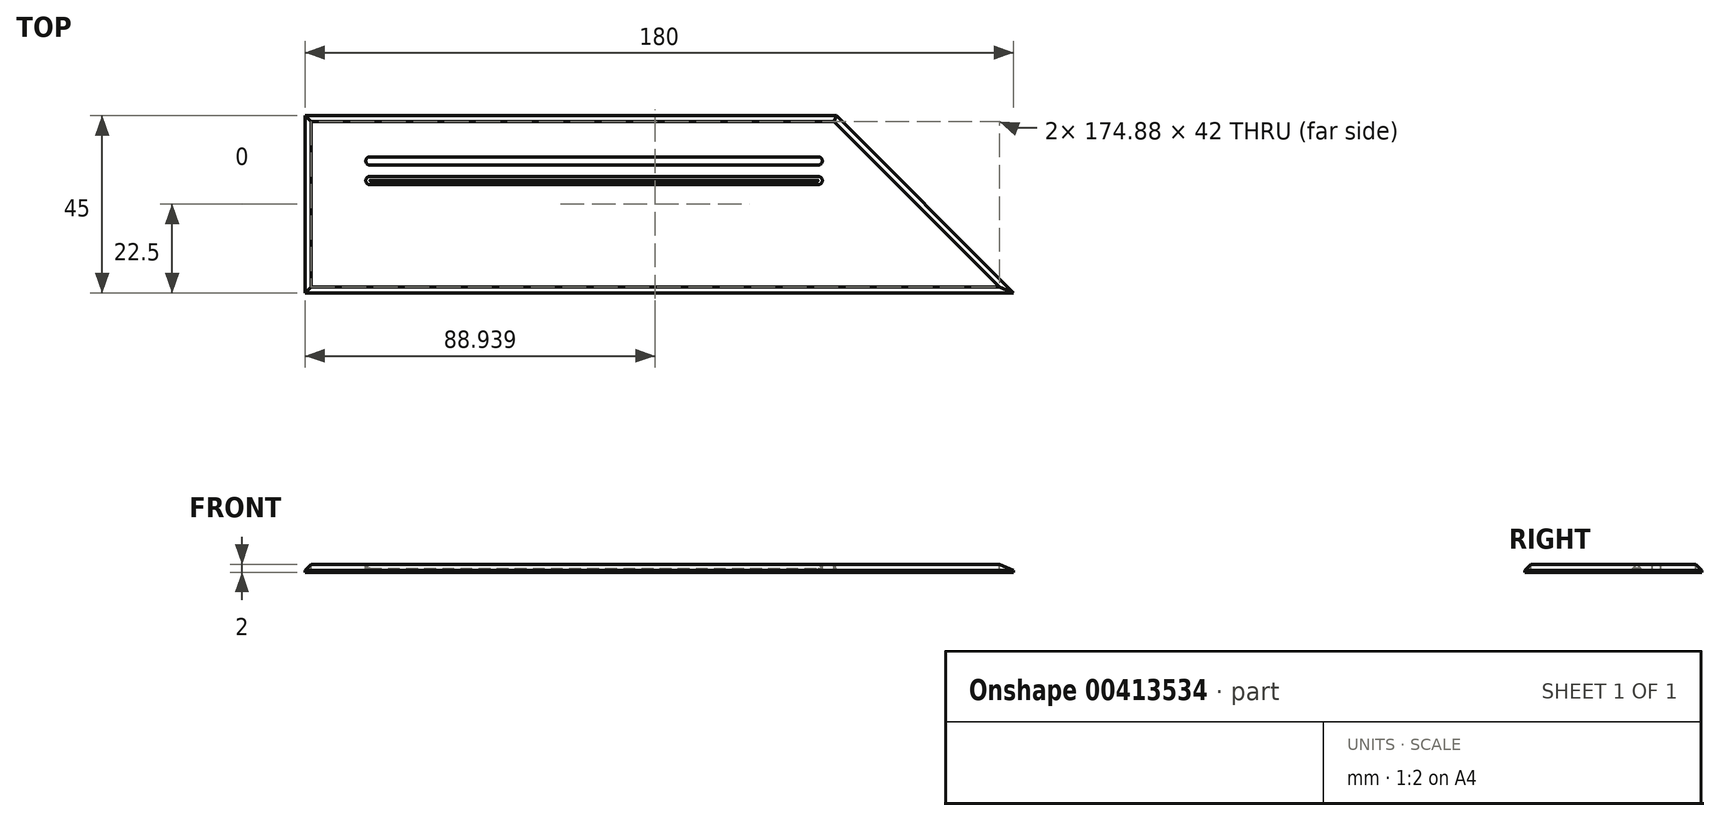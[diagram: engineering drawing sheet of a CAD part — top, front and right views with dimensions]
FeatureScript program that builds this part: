
annotation { "Feature Type Name" : "Feature", "Feature Type Description" : "" }
export const myFeature = defineFeature(function(context is Context, id is Id, definition is map)
    precondition{}
    {
        {
            var Q0;
            Q0=qCreatedBy(makeId("Top.planeOp"),FACE);
            var sketch = newSketch(context, id + "F0", { "sketchPlane" : qUnion([Q0])});
            skLineSegment(sketch, "E0.bottom", {"start": v(67.5, 22.5) * mm, "end": v(-67.5, 22.5) * mm});
            skLineSegment(sketch, "E0.top", {"start": v(112.5, -22.5) * mm, "end": v(-67.5, -22.5) * mm});
            skLineSegment(sketch, "E0.left", {"start": v(67.5, 22.5) * mm, "end": v(112.5, -22.5) * mm});
            skLineSegment(sketch, "E0.right", {"start": v(-67.5, 22.5) * mm, "end": v(-67.5, -22.5) * mm});
            skPoint(sketch, "E0.middle", {"position": v(0, 0) * mm});
            skSolve(sketch);
        }
        {
            var Q0;
            Q0=makeQuery(id+"F0.imprint","IMPRINT",FACE,{"disambiguationData":[TD([[makeQuery(id+"F0.imprint","IMPRINT",EDGE,{"derivedFrom":sQuery(id+"F0.wireOp",EDGE,"E0.bottom")}),1.0]])]});
            extrude(context, id + "F1", {"entities" : qUnion([Q0]), "depth" : 2 * mm});
        }
        {
            var Q0;
            Q0=makeQuery(id+"F1.opExtrude","CAP_EDGE",EDGE,{"disambiguationData":[OSD([sQuery(id+"F0.wireOp",EDGE,"E0.top")])],"isStart":false});
            var Q1;
            Q1=makeQuery(id+"F1.opExtrude","CAP_EDGE",EDGE,{"disambiguationData":[OSD([sQuery(id+"F0.wireOp",EDGE,"E0.right")])],"isStart":false});
            var Q2;
            Q2=makeQuery(id+"F1.opExtrude","CAP_EDGE",EDGE,{"disambiguationData":[OSD([sQuery(id+"F0.wireOp",EDGE,"E0.bottom")])],"isStart":false});
            var Q3;
            Q3=makeQuery(id+"F1.opExtrude","CAP_EDGE",EDGE,{"disambiguationData":[OSD([sQuery(id+"F0.wireOp",EDGE,"E0.left")])],"isStart":false});
            chamfer(context, id + "F2", {"entities" : qUnion([Q0, Q1, Q2, Q3]), "width" : 1.5 * mm, "tangentPropagation" : true});
        }
        {
            var Q0;
            Q0=makeQuery(id+"F1.opExtrude","CAP_FACE",FACE,{"disambiguationData":[OSD([sQuery(id+"F0.wireOp",EDGE,"E0.bottom"),sQuery(id+"F0.wireOp",EDGE,"E0.top"),sQuery(id+"F0.wireOp",EDGE,"E0.left"),sQuery(id+"F0.wireOp",EDGE,"E0.right")])],"isStart":false});
            var sketch = newSketch(context, id + "F3", { "sketchPlane" : qUnion([Q0])});
            skLineSegment(sketch, "E1", {"start": v(-51, 11) * mm, "end": v(62.88, 11) * mm, "construction": true});
            skLineSegment(sketch, "E2", {"start": v(-51, 6) * mm, "end": v(62.88, 6) * mm, "construction": true});
            skArc(sketch, "E3.0.startCap", {"start": v(-51, 9.95) * mm, "mid": v(-52.05, 11) * mm, "end": v(-51, 12.05) * mm});
            skArc(sketch, "E3.0.endCap", {"start": v(62.88, 12.05) * mm, "mid": v(63.93, 11) * mm, "end": v(62.88, 9.95) * mm});
            skLineSegment(sketch, "E3.0.left", {"start": v(-51, 12.05) * mm, "end": v(62.88, 12.05) * mm});
            skLineSegment(sketch, "E3.0.right", {"start": v(-51, 9.95) * mm, "end": v(62.88, 9.95) * mm});
            skArc(sketch, "E3.2.startCap", {"start": v(-51, 4.95) * mm, "mid": v(-52.05, 6) * mm, "end": v(-51, 7.05) * mm});
            skArc(sketch, "E3.2.endCap", {"start": v(62.88, 7.05) * mm, "mid": v(63.93, 6) * mm, "end": v(62.88, 4.95) * mm});
            skLineSegment(sketch, "E3.2.left", {"start": v(-51, 7.05) * mm, "end": v(62.88, 7.05) * mm});
            skLineSegment(sketch, "E3.2.right", {"start": v(-51, 4.95) * mm, "end": v(62.88, 4.95) * mm});
            skLineSegment(sketch, "E4", {"start": v(-51, -9) * mm, "end": v(92.88, -9) * mm, "construction": true});
            skCircle(sketch, "E5", {"center": v(-49, -9) * mm, "radius": 2 * mm});
            skCircle(sketch, "E6", {"center": v(-39, -9) * mm, "radius": 3 * mm});
            skCircle(sketch, "E7", {"center": v(-27, -9) * mm, "radius": 4 * mm});
            skCircle(sketch, "E8", {"center": v(-13, -9) * mm, "radius": 5 * mm});
            skCircle(sketch, "E9", {"center": v(3, -9) * mm, "radius": 6 * mm});
            skEllipse(sketch, "E10", {"center": v(19, -9) * mm, "majorRadius": 2.45 * mm, "minorRadius": 1.41 * mm, "majorAxis": v(-0.7, 0.7)});
            skLineSegment(sketch, "E11", {"start": v(19, -9) * mm, "end": v(17.27, -7.27) * mm, "construction": true});
            skLineSegment(sketch, "E12", {"start": v(21, -7) * mm, "end": v(18, -7) * mm, "construction": true});
            skLineSegment(sketch, "E13", {"start": v(21, -7) * mm, "end": v(21, -10) * mm, "construction": true});
            skEllipse(sketch, "E14", {"center": v(29, -9) * mm, "majorRadius": 3.67 * mm, "minorRadius": 2.12 * mm, "majorAxis": v(-0.7, 0.7)});
            skEllipse(sketch, "E15", {"center": v(42, -9) * mm, "majorRadius": 4.9 * mm, "minorRadius": 2.83 * mm, "majorAxis": v(-0.7, 0.7)});
            skEllipse(sketch, "E16", {"center": v(58, -9) * mm, "majorRadius": 6.12 * mm, "minorRadius": 3.54 * mm, "majorAxis": v(-0.7, 0.7)});
            skEllipse(sketch, "E17", {"center": v(76, -9) * mm, "majorRadius": 7.35 * mm, "minorRadius": 4.24 * mm, "majorAxis": v(-0.7, 0.7)});
            skLineSegment(sketch, "E18", {"start": v(32, -6) * mm, "end": v(27.5, -6) * mm, "construction": true});
            skLineSegment(sketch, "E19", {"start": v(32, -6) * mm, "end": v(32, -10.5) * mm, "construction": true});
            skLineSegment(sketch, "E20", {"start": v(40, -5) * mm, "end": v(46, -5) * mm, "construction": true});
            skLineSegment(sketch, "E21", {"start": v(46, -5) * mm, "end": v(46, -11) * mm, "construction": true});
            skLineSegment(sketch, "E22", {"start": v(55.5, -4) * mm, "end": v(63, -4) * mm, "construction": true});
            skLineSegment(sketch, "E23", {"start": v(63, -4) * mm, "end": v(63, -11.5) * mm, "construction": true});
            skLineSegment(sketch, "E24", {"start": v(73, -3) * mm, "end": v(82, -3) * mm, "construction": true});
            skLineSegment(sketch, "E25", {"start": v(82, -3) * mm, "end": v(82, -12) * mm, "construction": true});
            skLineSegment(sketch, "E26", {"start": v(29, -9) * mm, "end": v(26.4, -6.4) * mm, "construction": true});
            skLineSegment(sketch, "E27", {"start": v(42, -9) * mm, "end": v(38.54, -5.54) * mm, "construction": true});
            skLineSegment(sketch, "E28", {"start": v(58, -9) * mm, "end": v(53.67, -4.67) * mm, "construction": true});
            skLineSegment(sketch, "E29", {"start": v(76, -9) * mm, "end": v(70.8, -3.8) * mm, "construction": true});
            skLineSegment(sketch, "E30.bottom", {"start": v(-56, -6.5) * mm, "end": v(-61, -6.5) * mm});
            skLineSegment(sketch, "E30.top", {"start": v(-56, -11.5) * mm, "end": v(-61, -11.5) * mm});
            skLineSegment(sketch, "E30.left", {"start": v(-56, -6.5) * mm, "end": v(-56, -11.5) * mm});
            skLineSegment(sketch, "E30.right", {"start": v(-61, -6.5) * mm, "end": v(-61, -11.5) * mm});
            skLineSegment(sketch, "E31", {"start": v(-51, 11) * mm, "end": v(-51, -9) * mm, "construction": true});
            skLineSegment(sketch, "E32", {"start": v(62.88, 11) * mm, "end": v(62.88, 6) * mm, "construction": true});
            skLineSegment(sketch, "E33.bottom", {"start": v(-61, 11) * mm, "end": v(-56, 11) * mm});
            skLineSegment(sketch, "E33.top", {"start": v(-61, 6) * mm, "end": v(-56, 6) * mm});
            skLineSegment(sketch, "E33.left", {"start": v(-61, 11) * mm, "end": v(-61, 6) * mm});
            skLineSegment(sketch, "E33.right", {"start": v(-56, 11) * mm, "end": v(-56, 6) * mm});
            skSolve(sketch);
        }
        {
            var Q0;
            Q0=makeQuery(id+"F3.imprint","IMPRINT",FACE,{"disambiguationData":[TD([[makeQuery(id+"F3.imprint","IMPRINT",EDGE,{"derivedFrom":sQuery(id+"F3.wireOp",EDGE,"E33.bottom")}),-1.0]])]});
            var Q1;
            Q1=makeQuery(id+"F3.imprint","IMPRINT",FACE,{"disambiguationData":[TD([[makeQuery(id+"F3.imprint","IMPRINT",EDGE,{"derivedFrom":sQuery(id+"F3.wireOp",EDGE,"E3.0.startCap")}),-1.0]])]});
            var Q2;
            Q2=makeQuery(id+"F3.imprint","IMPRINT",FACE,{"disambiguationData":[TD([[makeQuery(id+"F3.imprint","IMPRINT",EDGE,{"derivedFrom":sQuery(id+"F3.wireOp",EDGE,"E3.2.startCap")}),-1.0]])]});
            var Q3;
            Q3=makeQuery(id+"F3.imprint","IMPRINT",FACE,{"disambiguationData":[TD([[makeQuery(id+"F3.imprint","IMPRINT",EDGE,{"derivedFrom":sQuery(id+"F3.wireOp",EDGE,"E30.bottom")}),1.0]])]});
            var Q4;
            Q4=makeQuery(id+"F3.imprint","IMPRINT",FACE,{"disambiguationData":[TD([[makeQuery(id+"F3.imprint","IMPRINT",EDGE,{"derivedFrom":sQuery(id+"F3.wireOp",EDGE,"E5")}),1.0]])]});
            var Q5;
            Q5=makeQuery(id+"F3.imprint","IMPRINT",FACE,{"disambiguationData":[TD([[makeQuery(id+"F3.imprint","IMPRINT",EDGE,{"derivedFrom":sQuery(id+"F3.wireOp",EDGE,"E6")}),1.0]])]});
            var Q6;
            Q6=makeQuery(id+"F3.imprint","IMPRINT",FACE,{"disambiguationData":[TD([[makeQuery(id+"F3.imprint","IMPRINT",EDGE,{"derivedFrom":sQuery(id+"F3.wireOp",EDGE,"E7")}),1.0]])]});
            var Q7;
            Q7=makeQuery(id+"F3.imprint","IMPRINT",FACE,{"disambiguationData":[TD([[makeQuery(id+"F3.imprint","IMPRINT",EDGE,{"derivedFrom":sQuery(id+"F3.wireOp",EDGE,"E8")}),1.0]])]});
            var Q8;
            Q8=makeQuery(id+"F3.imprint","IMPRINT",FACE,{"disambiguationData":[TD([[makeQuery(id+"F3.imprint","IMPRINT",EDGE,{"derivedFrom":sQuery(id+"F3.wireOp",EDGE,"E9")}),1.0]])]});
            var Q9;
            Q9=makeQuery(id+"F3.imprint","IMPRINT",FACE,{"disambiguationData":[TD([[makeQuery(id+"F3.imprint","IMPRINT",EDGE,{"derivedFrom":sQuery(id+"F3.wireOp",EDGE,"E10")}),1.0]])]});
            var Q10;
            Q10=makeQuery(id+"F3.imprint","IMPRINT",FACE,{"disambiguationData":[TD([[makeQuery(id+"F3.imprint","IMPRINT",EDGE,{"derivedFrom":sQuery(id+"F3.wireOp",EDGE,"E14")}),1.0]])]});
            var Q11;
            Q11=makeQuery(id+"F3.imprint","IMPRINT",FACE,{"disambiguationData":[TD([[makeQuery(id+"F3.imprint","IMPRINT",EDGE,{"derivedFrom":sQuery(id+"F3.wireOp",EDGE,"E15")}),1.0]])]});
            var Q12;
            Q12=makeQuery(id+"F3.imprint","IMPRINT",FACE,{"disambiguationData":[TD([[makeQuery(id+"F3.imprint","IMPRINT",EDGE,{"derivedFrom":sQuery(id+"F3.wireOp",EDGE,"E16")}),1.0]])]});
            var Q13;
            Q13=makeQuery(id+"F3.imprint","IMPRINT",FACE,{"disambiguationData":[TD([[makeQuery(id+"F3.imprint","IMPRINT",EDGE,{"derivedFrom":sQuery(id+"F3.wireOp",EDGE,"E17")}),1.0]])]});
            extrude(context, id + "F4", {"entities" : qUnion([Q0, Q1, Q2, Q3, Q4, Q5, Q6, Q7, Q8, Q9, Q10, Q11, Q12, Q13]), "operationType" : NewBodyOperationType.REMOVE, "oppositeDirection" : true, "depth" : 25 * mm});
        }
        {
            var Q0;
            Q0=makeQuery(id+"F4.boolean.opBoolean","COPY",EDGE,{"derivedFrom":makeQuery(id+"F4.opExtrude","CAP_EDGE",EDGE,{"disambiguationData":[OSD([sQuery(id+"F3.wireOp",EDGE,"2bolqe33-BX0B-IHgM-fZGM-oT8BxiQruySi")])],"isStart":true})});
            var Q1;
            Q1=makeQuery(id+"F4.boolean.opBoolean","COPY",EDGE,{"derivedFrom":makeQuery(id+"F4.opExtrude","CAP_EDGE",EDGE,{"disambiguationData":[OSD([sQuery(id+"F3.wireOp",EDGE,"E5")])],"isStart":true})});
            var Q2;
            Q2=makeQuery(id+"F4.boolean.opBoolean","COPY",EDGE,{"derivedFrom":makeQuery(id+"F4.opExtrude","CAP_EDGE",EDGE,{"disambiguationData":[OSD([sQuery(id+"F3.wireOp",EDGE,"E6")])],"isStart":true})});
            var Q3;
            Q3=makeQuery(id+"F4.boolean.opBoolean","COPY",EDGE,{"derivedFrom":makeQuery(id+"F4.opExtrude","CAP_EDGE",EDGE,{"disambiguationData":[OSD([sQuery(id+"F3.wireOp",EDGE,"E7")])],"isStart":true})});
            var Q4;
            Q4=makeQuery(id+"F4.boolean.opBoolean","COPY",EDGE,{"derivedFrom":makeQuery(id+"F4.opExtrude","CAP_EDGE",EDGE,{"disambiguationData":[OSD([sQuery(id+"F3.wireOp",EDGE,"E8")])],"isStart":true})});
            var Q5;
            Q5=makeQuery(id+"F4.boolean.opBoolean","COPY",EDGE,{"derivedFrom":makeQuery(id+"F4.opExtrude","CAP_EDGE",EDGE,{"disambiguationData":[OSD([sQuery(id+"F3.wireOp",EDGE,"E9")])],"isStart":true})});
            var Q6;
            Q6=makeQuery(id+"F4.boolean.opBoolean","COPY",EDGE,{"derivedFrom":makeQuery(id+"F4.opExtrude","CAP_EDGE",EDGE,{"disambiguationData":[OSD([sQuery(id+"F3.wireOp",EDGE,"E10")])],"isStart":true})});
            var Q7;
            Q7=makeQuery(id+"F4.boolean.opBoolean","COPY",EDGE,{"derivedFrom":makeQuery(id+"F4.opExtrude","CAP_EDGE",EDGE,{"disambiguationData":[OSD([sQuery(id+"F3.wireOp",EDGE,"E14")])],"isStart":true})});
            var Q8;
            Q8=makeQuery(id+"F4.boolean.opBoolean","COPY",EDGE,{"derivedFrom":makeQuery(id+"F4.opExtrude","CAP_EDGE",EDGE,{"disambiguationData":[OSD([sQuery(id+"F3.wireOp",EDGE,"E15")])],"isStart":true})});
            var Q9;
            Q9=makeQuery(id+"F4.boolean.opBoolean","COPY",EDGE,{"derivedFrom":makeQuery(id+"F4.opExtrude","CAP_EDGE",EDGE,{"disambiguationData":[OSD([sQuery(id+"F3.wireOp",EDGE,"E16")])],"isStart":true})});
            var Q10;
            Q10=makeQuery(id+"F4.boolean.opBoolean","COPY",EDGE,{"derivedFrom":makeQuery(id+"F4.opExtrude","CAP_EDGE",EDGE,{"disambiguationData":[OSD([sQuery(id+"F3.wireOp",EDGE,"E17")])],"isStart":true})});
            var Q11;
            Q11=makeQuery(id+"F4.boolean.opBoolean","COPY",EDGE,{"derivedFrom":makeQuery(id+"F4.opExtrude","CAP_EDGE",EDGE,{"disambiguationData":[OSD([sQuery(id+"F3.wireOp",EDGE,"E3.4.right")])],"isStart":true})});
            var Q12;
            Q12=makeQuery(id+"F4.boolean.opBoolean","COPY",EDGE,{"derivedFrom":makeQuery(id+"F4.opExtrude","CAP_EDGE",EDGE,{"disambiguationData":[OSD([sQuery(id+"F3.wireOp",EDGE,"E3.3.right")])],"isStart":true})});
            var Q13;
            Q13=makeQuery(id+"F4.boolean.opBoolean","COPY",EDGE,{"derivedFrom":makeQuery(id+"F4.opExtrude","CAP_EDGE",EDGE,{"disambiguationData":[OSD([sQuery(id+"F3.wireOp",EDGE,"E3.2.right")])],"isStart":true})});
            var Q14;
            Q14=makeQuery(id+"F4.boolean.opBoolean","COPY",EDGE,{"derivedFrom":makeQuery(id+"F4.opExtrude","CAP_EDGE",EDGE,{"disambiguationData":[OSD([sQuery(id+"F3.wireOp",EDGE,"E3.0.right")])],"isStart":true})});
            var Q15;
            Q15=makeQuery(id+"F4.boolean.opBoolean","COPY",EDGE,{"derivedFrom":makeQuery(id+"F4.opExtrude","CAP_EDGE",EDGE,{"disambiguationData":[OSD([sQuery(id+"F3.wireOp",EDGE,"E3.1.right")])],"isStart":true})});
            var Q16;
            Q16=makeQuery(id+"F4.boolean.opBoolean","COPY",EDGE,{"derivedFrom":makeQuery(id+"F4.opExtrude","CAP_EDGE",EDGE,{"disambiguationData":[OSD([sQuery(id+"F3.wireOp",EDGE,"E30.top")])],"isStart":true})});
            var Q17;
            Q17=makeQuery(id+"F4.boolean.opBoolean","COPY",EDGE,{"derivedFrom":makeQuery(id+"F4.opExtrude","CAP_EDGE",EDGE,{"disambiguationData":[OSD([sQuery(id+"F3.wireOp",EDGE,"E30.right")])],"isStart":true})});
            var Q18;
            Q18=makeQuery(id+"F4.boolean.opBoolean","COPY",EDGE,{"derivedFrom":makeQuery(id+"F4.opExtrude","CAP_EDGE",EDGE,{"disambiguationData":[OSD([sQuery(id+"F3.wireOp",EDGE,"E30.bottom")])],"isStart":true})});
            var Q19;
            Q19=makeQuery(id+"F4.boolean.opBoolean","COPY",EDGE,{"derivedFrom":makeQuery(id+"F4.opExtrude","CAP_EDGE",EDGE,{"disambiguationData":[OSD([sQuery(id+"F3.wireOp",EDGE,"E30.left")])],"isStart":true})});
            var Q20;
            Q20=makeQuery(id+"F4.boolean.opBoolean","COPY",EDGE,{"derivedFrom":makeQuery(id+"F4.opExtrude","CAP_EDGE",EDGE,{"disambiguationData":[OSD([sQuery(id+"F3.wireOp",EDGE,"E33.top")])],"isStart":true})});
            var Q21;
            Q21=makeQuery(id+"F4.boolean.opBoolean","COPY",EDGE,{"derivedFrom":makeQuery(id+"F4.opExtrude","CAP_EDGE",EDGE,{"disambiguationData":[OSD([sQuery(id+"F3.wireOp",EDGE,"E33.right")])],"isStart":true})});
            var Q22;
            Q22=makeQuery(id+"F4.boolean.opBoolean","COPY",EDGE,{"derivedFrom":makeQuery(id+"F4.opExtrude","CAP_EDGE",EDGE,{"disambiguationData":[OSD([sQuery(id+"F3.wireOp",EDGE,"E33.bottom")])],"isStart":true})});
            var Q23;
            Q23=makeQuery(id+"F4.boolean.opBoolean","COPY",EDGE,{"derivedFrom":makeQuery(id+"F4.opExtrude","CAP_EDGE",EDGE,{"disambiguationData":[OSD([sQuery(id+"F3.wireOp",EDGE,"E33.left")])],"isStart":true})});
            chamfer(context, id + "F5", {"entities" : qUnion([Q0, Q1, Q2, Q3, Q4, Q5, Q6, Q7, Q8, Q9, Q10, Q11, Q12, Q13, Q14, Q15, Q16, Q17, Q18, Q19, Q20, Q21, Q22, Q23]), "width" : 1 * mm, "tangentPropagation" : true});
        }
    });
